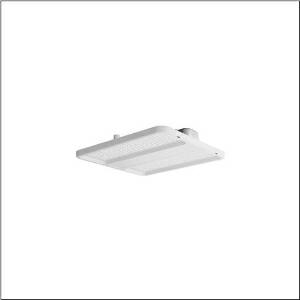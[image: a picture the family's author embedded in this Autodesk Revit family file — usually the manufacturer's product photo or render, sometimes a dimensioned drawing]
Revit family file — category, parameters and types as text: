
# Revit family: highbay_11_midi_51hn11da4hda
name_source: partatom
category: Lighting Fixtures
units: mm (PartAtom-declared; Revit-internal decimal feet)

## family parameters
Cut with Voids When Loaded = No
Host = Face
Light Source = No
Part Type = Normal
Room Calculation Point = No
Round Connector Dimension = Use Diameter
Shared = No

## types (1)
- --- (1 x LED, 2890 lm, 14.5 W, 4000K)
    Apparent Load = 15 VA
    CIE Flux Codes = 85 97 100 100 100
    Color Rendering = 80
    Color Temperature = 4000K
    Default Elevation = 1800 mm
    Description = high bay luminaire Highbay 11 midi; direct symmetric narrow distribution, light control with lens of PMMA; UGR ≤ 22 (X = 4H | Y = 8H | S = 0.25H | reflection values 70/50/20); luminous flux: 18.500lm; light colour: 840, colour temperature: 4000K, MacAdam ≤ 2 SDCM (initial), colour rendering: CRI > 80; luminous efficacy: 201,5lm/W; rated service life: 100.000h (L95) at AT= 25°C; control: DALI 2; luminaire connection: terminal, 5-pole, max. 2.5mm² (cable entry for one cable, Ø 8.5..16mm); mains connection: 230..240V, AC/DC 0/50..60Hz; connected load: 91,8W; protection rating (complete): IP66; insulation class (complete): insulation class I (protective earthing); protection symbol: D; impact resistance: IK08; certification: CE, ENEC, VDE, UKCA; luminaire for central battery installations according to EN 60598-2-22, internal wiring halogen-free; luminaire Suitable for use in the food industry according to the specifications of IFS-Food, HACCP and/or BRC; LABS conformity tested according to VDMA 24364:2018-05; housing frame of high-performance plastic PA6, matt traffic white (RAL 9016); cover of PMMA; dimension (LxWxH): 474 x 442 x 72mm; permissible operating ambient temperature: -40..+60°C (reducing of maximum allowable ambient temperature of 5°C with ceiling mounting); packaging unit: 1 piece; (delivery without accessories; please order mounting accessories separately)
    Height = 72 mm  [stored 0.23622 ft]
    Lamp = 1 x LED
    Lamp Light Flux = 2890 lm
    Lamp Power = 14.5 W
    Lamp count = 1
    Length = 474 mm
    Luminous efficacy = 199 lm/W
    Manufacturer = Siteco
    ModVariant = No
    Model = 51HN11DA4HDA
    Mounting Place = Ceiling
    Mounting Type = Pendant
    Number of Poles = 1
    OnlyDefault = Yes
    Power Factor = 1
    Product Name = Highbay 11 midi
    Product group = high bay luminaire
    ProductGroupID = 902
    Protection Class = Protection class I
    Protection Degree = IP 66
    RLX_Detail_Level = 1
    RLX_Emergency_Light_Flux = 0 lm
    RLX_Emergency_Type = 0
    RLX_Emergency_Type_DB = No
    RlxData = <blob elided: 75689 chars, md5=d9ea43ad>
    Socket = socket
    Standby Power = 0 W
    System Light Flux = 2890 lm
    System Power = 15 W
    Type Comments = : DC mode (central or group accumulator) initial emergency light level
    Type Image = l_1363240.jpg
    URL = http://relux.com
    VarID = @adj_022175
    Voltage = 0 V
    Weight = 0.00 kg
    Width = 442 mm

note: [stored X ft] marks values corroborated as IEEE doubles in the binary element streams (Revit-internal decimal feet)

## geometry (parser evidence)
native form markers: Blend x4, Sweep x9
no freeform markers — native parametric forms only
